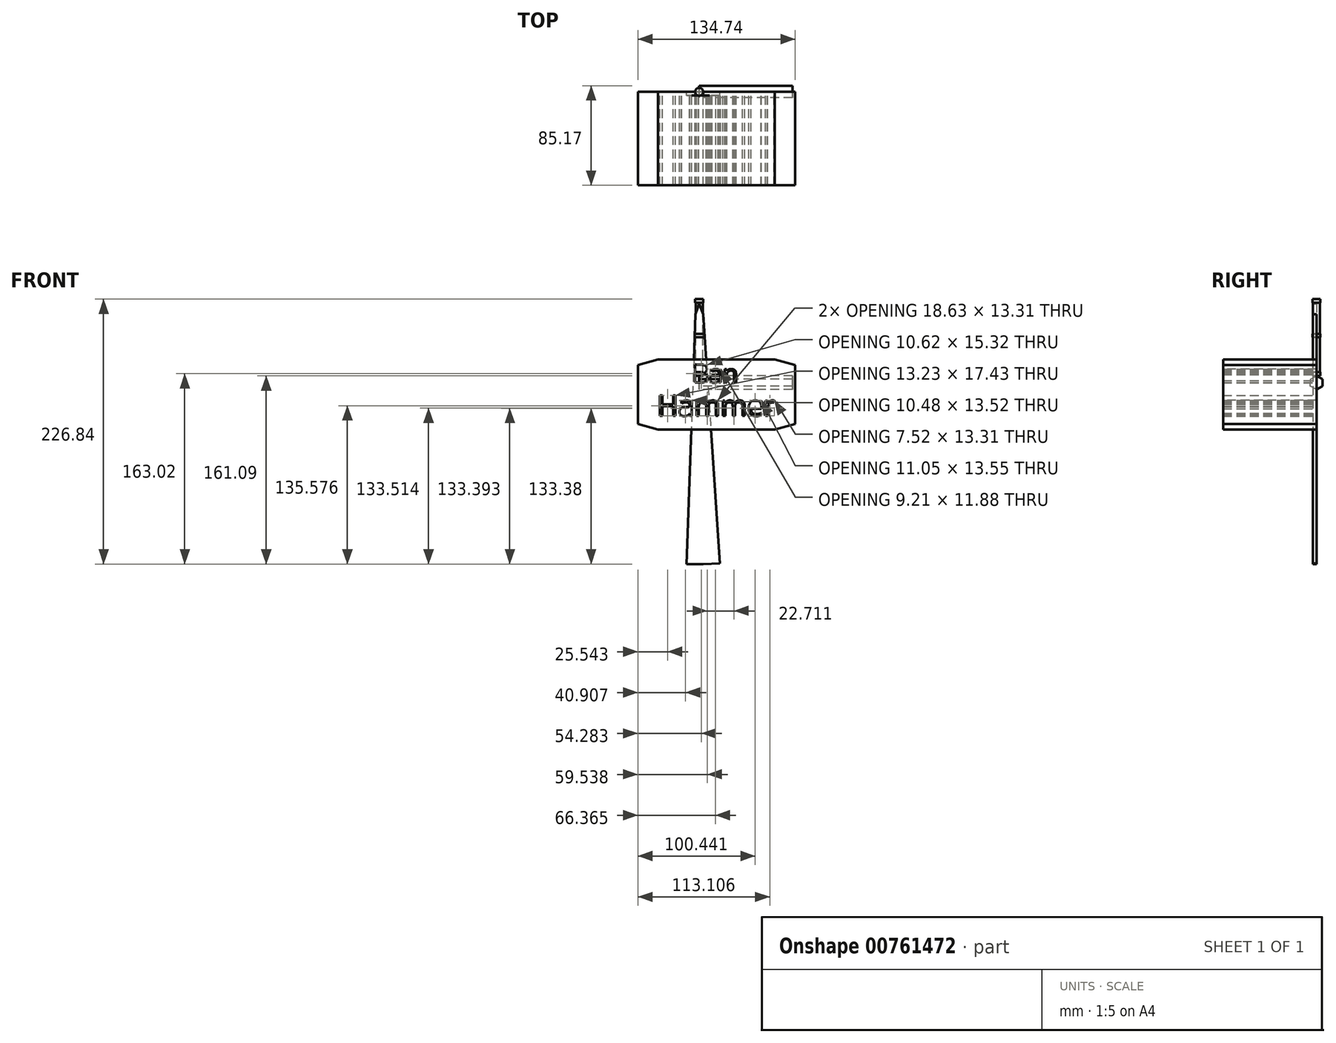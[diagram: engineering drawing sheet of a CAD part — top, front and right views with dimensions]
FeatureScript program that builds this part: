
annotation { "Feature Type Name" : "Feature", "Feature Type Description" : "" }
export const myFeature = defineFeature(function(context is Context, id is Id, definition is map)
    precondition{}
    {
        {
            var Q0;
            Q0=qCreatedBy(makeId("Front.planeOp"),FACE);
            var sketch = newSketch(context, id + "F0", { "sketchPlane" : qUnion([Q0])});
            skLineSegment(sketch, "E0.top", {"start": v(-3, 71.48) * mm, "end": v(0, 71.48) * mm});
            skLineSegment(sketch, "E1.bottom", {"start": v(-3, 71.48) * mm, "end": v(-3, 71.48) * mm});
            skLineSegment(sketch, "E1.top", {"start": v(-3, 68.48) * mm, "end": v(-3, 68.48) * mm});
            skLineSegment(sketch, "E2.right", {"start": v(0, 68.48) * mm, "end": v(0, 68.48) * mm});
            skLineSegment(sketch, "E3", {"start": v(-3, 68.48) * mm, "end": v(-3, 41.86) * mm});
            skLineSegment(sketch, "E4", {"start": v(-3, 38.98) * mm, "end": v(-3, 8.98) * mm});
            skLineSegment(sketch, "E5", {"start": v(-3, 5.98) * mm, "end": v(0, 5.98) * mm});
            skLineSegment(sketch, "E6", {"start": v(0, 71.48) * mm, "end": v(0, 5.98) * mm});
            skLineSegment(sketch, "E7", {"start": v(-3, 8.98) * mm, "end": v(-3.4, 8.98) * mm});
            skLineSegment(sketch, "E8", {"start": v(-3, 5.98) * mm, "end": v(-3.4, 5.98) * mm});
            skLineSegment(sketch, "E9", {"start": v(-3.4, 8.98) * mm, "end": v(-3.4, 5.98) * mm});
            skLineSegment(sketch, "E10", {"start": v(-3, 41.86) * mm, "end": v(-3.4, 41.86) * mm});
            skLineSegment(sketch, "E11", {"start": v(-3, 38.98) * mm, "end": v(-3.4, 38.98) * mm});
            skLineSegment(sketch, "E12", {"start": v(-3.4, 38.98) * mm, "end": v(-3.4, 41.86) * mm});
            skLineSegment(sketch, "E13", {"start": v(-3, 71.48) * mm, "end": v(-3.4, 71.48) * mm});
            skLineSegment(sketch, "E14", {"start": v(-3.4, 71.48) * mm, "end": v(-3.4, 68.48) * mm});
            skLineSegment(sketch, "E15", {"start": v(-3.4, 68.48) * mm, "end": v(-3, 68.48) * mm});
            skPoint(sketch, "E16.end.orphan", {"position": v(0, 41.86) * mm});
            skPoint(sketch, "E17.end.orphan", {"position": v(0, 38.98) * mm});
            skPoint(sketch, "E18.end.orphan", {"position": v(0, 28.35) * mm});
            skSolve(sketch);
        }
        {
            var Q0;
            Q0=makeQuery(id+"F0.imprint","IMPRINT",FACE,{"disambiguationData":[TD([[makeQuery(id+"F0.imprint","IMPRINT",EDGE,{"derivedFrom":sQuery(id+"F0.wireOp",EDGE,"E0.top")}),-1.0]])]});
            var Q1;
            Q1=sQuery(id+"F0.wireOp",EDGE,"E6");
            revolve(context, id + "F1", {"surfaceOperationType" : NewSurfaceOperationType.NEW, "entities" : qUnion([Q0]), "axis" : qUnion([Q1]), "revolveType" : RevolveType.FULL});
        }
        {
            var Q0;
            Q0=qCreatedBy(makeId("Right.planeOp"),FACE);
            var sketch = newSketch(context, id + "F2", { "sketchPlane" : qUnion([Q0])});
            skCircle(sketch, "E19.cCircle", {"center": v(0, 0) * mm, "radius": 5.16 * mm, "construction": true});
            skLineSegment(sketch, "E19.0", {"start": v(0.02, 5.95) * mm, "end": v(5.17, 2.96) * mm});
            skLineSegment(sketch, "E19.1", {"start": v(5.17, 2.96) * mm, "end": v(5.15, -3) * mm});
            skLineSegment(sketch, "E19.2", {"start": v(5.15, -3) * mm, "end": v(-0.02, -5.95) * mm});
            skLineSegment(sketch, "E19.3", {"start": v(-0.02, -5.95) * mm, "end": v(-5.17, -2.96) * mm});
            skLineSegment(sketch, "E19.4", {"start": v(-5.17, -2.96) * mm, "end": v(-5.15, 3) * mm});
            skLineSegment(sketch, "E19.5", {"start": v(-5.15, 3) * mm, "end": v(0.02, 5.95) * mm});
            skPoint(sketch, "E19.0.midPoint", {"position": v(2.6, 4.46) * mm});
            skSolve(sketch);
        }
        {
            var Q0;
            Q0=makeQuery(id+"F2.imprint","IMPRINT",FACE,{"disambiguationData":[TD([[makeQuery(id+"F2.imprint","IMPRINT",EDGE,{"derivedFrom":sQuery(id+"F2.wireOp",EDGE,"E19.0")}),-1.0]])]});
            extrude(context, id + "F3", {"entities" : qUnion([Q0]), "depth" : 80 * mm, "offsetDistance" : 25 * mm});
        }
        {
            var Q0;
            Q0=qCreatedBy(makeId("Front.planeOp"),FACE);
            var sketch = newSketch(context, id + "F4", { "sketchPlane" : qUnion([Q0])});
            skLineSegment(sketch, "E20", {"start": v(0, 67.6) * mm, "end": v(-3.18, 58.52) * mm});
            skLineSegment(sketch, "E21.MirrorCS", {"start": v(0, 67.6) * mm, "end": v(3.46, 58.62) * mm});
            skPoint(sketch, "E22.orphan", {"position": v(0, -30.03) * mm});
            skLineSegment(sketch, "E23", {"start": v(-3.18, 58.52) * mm, "end": v(-10.9, -155.36) * mm});
            skLineSegment(sketch, "E24", {"start": v(-10.9, -155.36) * mm, "end": v(3.46, -155.36) * mm});
            skLineSegment(sketch, "E25.MirrorCS", {"start": v(3.46, 58.62) * mm, "end": v(17.83, -154.92) * mm});
            skLineSegment(sketch, "E26.MirrorCS", {"start": v(17.83, -154.92) * mm, "end": v(3.46, -155.36) * mm});
            skSolve(sketch);
        }
        {
            var Q0;
            Q0=makeQuery(id+"F4.imprint","IMPRINT",FACE,{"disambiguationData":[TD([[makeQuery(id+"F4.imprint","IMPRINT",EDGE,{"derivedFrom":sQuery(id+"F4.wireOp",EDGE,"E20")}),1.0]])]});
            var Q1;
            {var subQ0=sQuery(id+"F4.wireOp",EDGE,"54EJ6phU-Mi66-ZMGN-6utl-2kP9IqacGzZd");Q1=makeQuery(id+"F4.imprint","IMPRINT",FACE,{"disambiguationData":[TD([[makeQuery(id+"F4.imprint","IMPRINT",EDGE,{"derivedFrom":subQ0}),-1.0]])]});}
            extrude(context, id + "F5", {"entities" : qUnion([Q0, Q1]), "depth" : 3 * mm, "offsetDistance" : 25 * mm});
        }
        {
            var Q0;
            Q0=qCreatedBy(makeId("Front.planeOp"),FACE);
            var sketch = newSketch(context, id + "F6", { "sketchPlane" : qUnion([Q0])});
            skLineSegment(sketch, "E27.bottom", {"start": v(-35.22, 19.89) * mm, "end": v(64.78, 19.89) * mm});
            skLineSegment(sketch, "E27.top", {"start": v(-35.22, -40.11) * mm, "end": v(64.78, -40.11) * mm});
            skLineSegment(sketch, "E27.left", {"start": v(-35.22, 19.89) * mm, "end": v(-35.22, -40.11) * mm});
            skLineSegment(sketch, "E27.right", {"start": v(64.78, 19.89) * mm, "end": v(64.78, -40.11) * mm});
            skLineSegment(sketch, "E28", {"start": v(-35.22, 19.89) * mm, "end": v(-52.57, 15.07) * mm});
            skLineSegment(sketch, "E29", {"start": v(-52.57, 15.07) * mm, "end": v(-52.57, -35.3) * mm});
            skLineSegment(sketch, "E30", {"start": v(-52.57, -35.3) * mm, "end": v(-35.22, -40.11) * mm});
            skLineSegment(sketch, "E31", {"start": v(64.78, 19.89) * mm, "end": v(82.13, 15.1) * mm});
            skLineSegment(sketch, "E32", {"start": v(64.78, -40.11) * mm, "end": v(82.17, -35.46) * mm});
            skLineSegment(sketch, "E33", {"start": v(82.13, 15.1) * mm, "end": v(82.17, -35.46) * mm});
            skText(sketch, "E34", { "text": "Ban", "fontName": "OpenSans-Regular.ttf"});
            skText(sketch, "E35", { "text": "Hammer", "fontName": "OpenSans-Regular.ttf"});
            const initialGuessF6  = {"E34": [-0.0057, 0, 1, 0, 0.01545], "E35": [-0.03604, -0.0285, 1, 0, 0.01758]};
            skSetInitialGuess(sketch, initialGuessF6);
            skSolve(sketch);
        }
        {
            var Q0;
            Q0=makeQuery(id+"F6.imprint","IMPRINT",FACE,{"disambiguationData":[TD([[makeQuery(id+"F6.imprint","IMPRINT",EDGE,{"derivedFrom":sQuery(id+"F6.wireOp",EDGE,"E27.left")}),-1.0]])]});
            var Q1;
            Q1=makeQuery(id+"F6.imprint","IMPRINT",FACE,{"disambiguationData":[TD([[makeQuery(id+"F6.imprint","IMPRINT",EDGE,{"derivedFrom":sQuery(id+"F6.wireOp",EDGE,"E27.right")}),1.0]])]});
            var Q2;
            Q2=makeQuery(id+"F6.imprint","IMPRINT",FACE,{"disambiguationData":[TD([[makeQuery(id+"F6.imprint","IMPRINT",EDGE,{"derivedFrom":sQuery(id+"F6.wireOp",EDGE,"E27.bottom")}),-1.0]])]});
            extrude(context, id + "F7", {"entities" : qUnion([Q0, Q1, Q2]), "depth" : 80 * mm, "offsetDistance" : 25 * mm});
        }
    });
